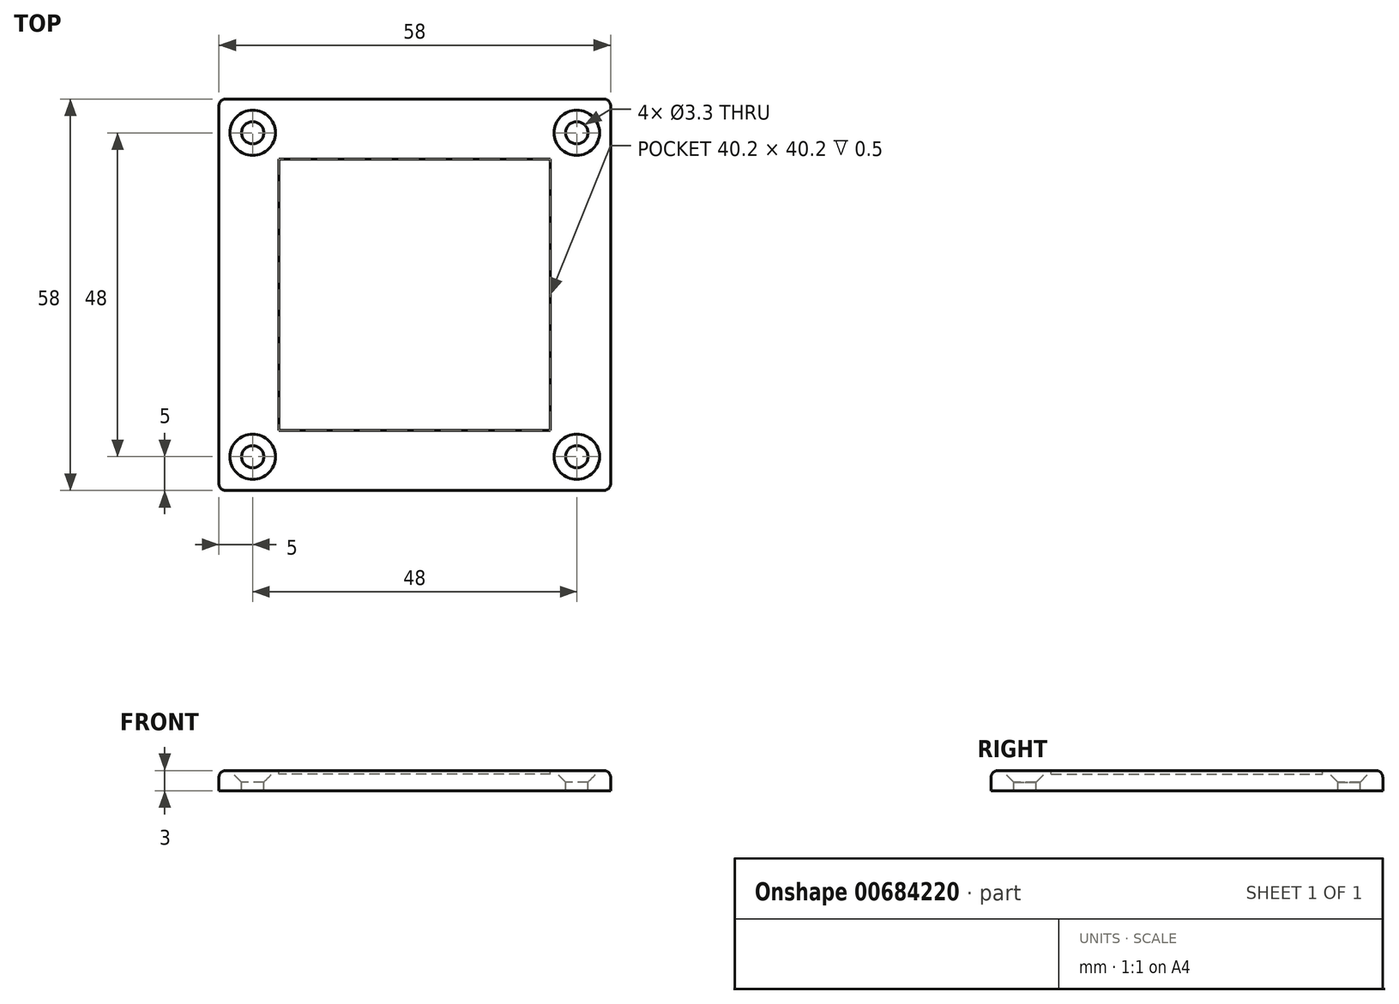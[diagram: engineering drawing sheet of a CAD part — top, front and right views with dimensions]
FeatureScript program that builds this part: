
annotation { "Feature Type Name" : "Feature", "Feature Type Description" : "" }
export const myFeature = defineFeature(function(context is Context, id is Id, definition is map)
    precondition{}
    {
        {
            var Q0;
            Q0=qCreatedBy(makeId("Top.planeOp"),FACE);
            var sketch = newSketch(context, id + "F0", { "sketchPlane" : qUnion([Q0])});
            skLineSegment(sketch, "E0.bottom", {"start": v(28, -29) * mm, "end": v(-28, -29) * mm});
            skLineSegment(sketch, "E0.top", {"start": v(28, 29) * mm, "end": v(-28, 29) * mm});
            skLineSegment(sketch, "E0.left", {"start": v(29, -28) * mm, "end": v(29, 28) * mm});
            skLineSegment(sketch, "E0.right", {"start": v(-29, -28) * mm, "end": v(-29, 28) * mm});
            skPoint(sketch, "E0.middle", {"position": v(0, 0) * mm});
            skPoint(sketch, "E1.visualSharp", {"position": v(-29, 29) * mm});
            skArc(sketch, "E1.filletArc", {"start": v(-28, 29) * mm, "mid": v(-28.7, 28.7) * mm, "end": v(-29, 28) * mm});
            skPoint(sketch, "E2.visualSharp", {"position": v(29, 29) * mm});
            skArc(sketch, "E2.filletArc", {"start": v(29, 28) * mm, "mid": v(28.7, 28.7) * mm, "end": v(28, 29) * mm});
            skPoint(sketch, "E3.visualSharp", {"position": v(29, -29) * mm});
            skArc(sketch, "E3.filletArc", {"start": v(28, -29) * mm, "mid": v(28.7, -28.7) * mm, "end": v(29, -28) * mm});
            skPoint(sketch, "E4.visualSharp", {"position": v(-29, -29) * mm});
            skArc(sketch, "E4.filletArc", {"start": v(-29, -28) * mm, "mid": v(-28.7, -28.7) * mm, "end": v(-28, -29) * mm});
            skSolve(sketch);
        }
        {
            var Q0;
            Q0 = qSketchRegion(id + "F0", true);
            extrude(context, id + "F1", {"entities" : qUnion([Q0]), "depth" : 3 * mm, "offsetDistance" : 25 * mm});
        }
        {
            var Q0;
            Q0=makeQuery(id+"F1.opExtrude","CAP_EDGE",EDGE,{"disambiguationData":[OSD([sQuery(id+"F0.wireOp",EDGE,"E0.left")])],"isStart":false});
            fillet(context, id + "F2", {"entities" : qUnion([Q0]), "radius" : 1 * mm, "tangentPropagation" : true, "allowEdgeOverflow" : false});
        }
        {
            var Q0;
            Q0=makeQuery(id+"F1.opExtrude","CAP_FACE",FACE,{"disambiguationData":[OSD([sQuery(id+"F0.wireOp",EDGE,"E0.bottom"),sQuery(id+"F0.wireOp",EDGE,"E0.top"),sQuery(id+"F0.wireOp",EDGE,"E0.left"),sQuery(id+"F0.wireOp",EDGE,"E0.right"),sQuery(id+"F0.wireOp",EDGE,"E1.filletArc"),sQuery(id+"F0.wireOp",EDGE,"E2.filletArc"),sQuery(id+"F0.wireOp",EDGE,"E3.filletArc"),sQuery(id+"F0.wireOp",EDGE,"E4.filletArc")])],"isStart":false});
            var sketch = newSketch(context, id + "F3", { "sketchPlane" : qUnion([Q0])});
            skLineSegment(sketch, "E5.bottom", {"start": v(24, -24) * mm, "end": v(-24, -24) * mm, "construction": true});
            skLineSegment(sketch, "E5.top", {"start": v(24, 24) * mm, "end": v(-24, 24) * mm, "construction": true});
            skLineSegment(sketch, "E5.left", {"start": v(24, -24) * mm, "end": v(24, 24) * mm, "construction": true});
            skLineSegment(sketch, "E5.right", {"start": v(-24, -24) * mm, "end": v(-24, 24) * mm, "construction": true});
            skPoint(sketch, "E5.middle", {"position": v(0, 0) * mm});
            skPoint(sketch, "E6", {"position": v(-24, 24) * mm});
            skPoint(sketch, "E7", {"position": v(24, 24) * mm});
            skPoint(sketch, "E8", {"position": v(24, -24) * mm});
            skPoint(sketch, "E9", {"position": v(-24, -24) * mm});
            skSolve(sketch);
        }
        {
            var Q0;
            Q0=sQuery(id+"F3.wireOp",VERTEX,"E6");
            var Q1;
            Q1=sQuery(id+"F3.wireOp",VERTEX,"E7");
            var Q2;
            Q2=sQuery(id+"F3.wireOp",VERTEX,"E9");
            var Q3;
            Q3=sQuery(id+"F3.wireOp",VERTEX,"E8");
            var Q4;
            Q4=makeQuery(id+"F1.opExtrude","SWEPT_BODY",BODY,{"disambiguationData":[OSD([sQuery(id+"F0.wireOp",EDGE,"E0.bottom"),sQuery(id+"F0.wireOp",EDGE,"E0.top"),sQuery(id+"F0.wireOp",EDGE,"E0.left"),sQuery(id+"F0.wireOp",EDGE,"E0.right"),sQuery(id+"F0.wireOp",EDGE,"E1.filletArc"),sQuery(id+"F0.wireOp",EDGE,"E2.filletArc"),sQuery(id+"F0.wireOp",EDGE,"E3.filletArc"),sQuery(id+"F0.wireOp",EDGE,"E4.filletArc")])]});
            hole(context, id + "F4", {"style" : HoleStyle.C_SINK, "endStyle" : HoleEndStyle.THROUGH, "standardTappedOrClearance" : lookupTablePath({ "standard" : "ISO", "fit" : "Normal", "size" : "M3", "type" : "Clearance" }), "standardBlindInLast" : lookupTablePath({ "fit" : "Standard", "standard" : "ISO", "size" : "M3", "type" : "Clearance" }), "holeDiameter" : 3.3 * mm, "cSinkDiameter" : 6.72 * mm, "cSinkAngle" : 90 * degree, "majorDiameter" : 5 * mm, "tappedDepth" : 8 * mm, "tapClearance" : 3, "startFromSketch" : true, "locations" : qUnion([Q0, Q1, Q2, Q3]), "scope" : qUnion([Q4])});
        }
        {
            var Q0;
            Q0=makeQuery(id+"F1.opExtrude","CAP_FACE",FACE,{"disambiguationData":[OSD([sQuery(id+"F0.wireOp",EDGE,"E0.bottom"),sQuery(id+"F0.wireOp",EDGE,"E0.top"),sQuery(id+"F0.wireOp",EDGE,"E0.left"),sQuery(id+"F0.wireOp",EDGE,"E0.right"),sQuery(id+"F0.wireOp",EDGE,"E1.filletArc"),sQuery(id+"F0.wireOp",EDGE,"E2.filletArc"),sQuery(id+"F0.wireOp",EDGE,"E3.filletArc"),sQuery(id+"F0.wireOp",EDGE,"E4.filletArc")])],"isStart":false});
            var sketch = newSketch(context, id + "F5", { "sketchPlane" : qUnion([Q0])});
            skLineSegment(sketch, "E10.bottom", {"start": v(20.1, -20.1) * mm, "end": v(-20.1, -20.1) * mm});
            skLineSegment(sketch, "E10.top", {"start": v(20.1, 20.1) * mm, "end": v(-20.1, 20.1) * mm});
            skLineSegment(sketch, "E10.left", {"start": v(20.1, -20.1) * mm, "end": v(20.1, 20.1) * mm});
            skLineSegment(sketch, "E10.right", {"start": v(-20.1, -20.1) * mm, "end": v(-20.1, 20.1) * mm});
            skPoint(sketch, "E10.middle", {"position": v(0, 0) * mm});
            skSolve(sketch);
        }
        {
            var Q0;
            Q0=makeQuery(id+"F5.imprint","IMPRINT",FACE,{"disambiguationData":[TD([[makeQuery(id+"F5.imprint","IMPRINT",EDGE,{"derivedFrom":sQuery(id+"F5.wireOp",EDGE,"E10.bottom")}),-1.0]])]});
            extrude(context, id + "F6", {"entities" : qUnion([Q0]), "operationType" : NewBodyOperationType.REMOVE, "oppositeDirection" : true, "depth" : 0.5 * mm, "offsetDistance" : 25 * mm});
        }
    });
